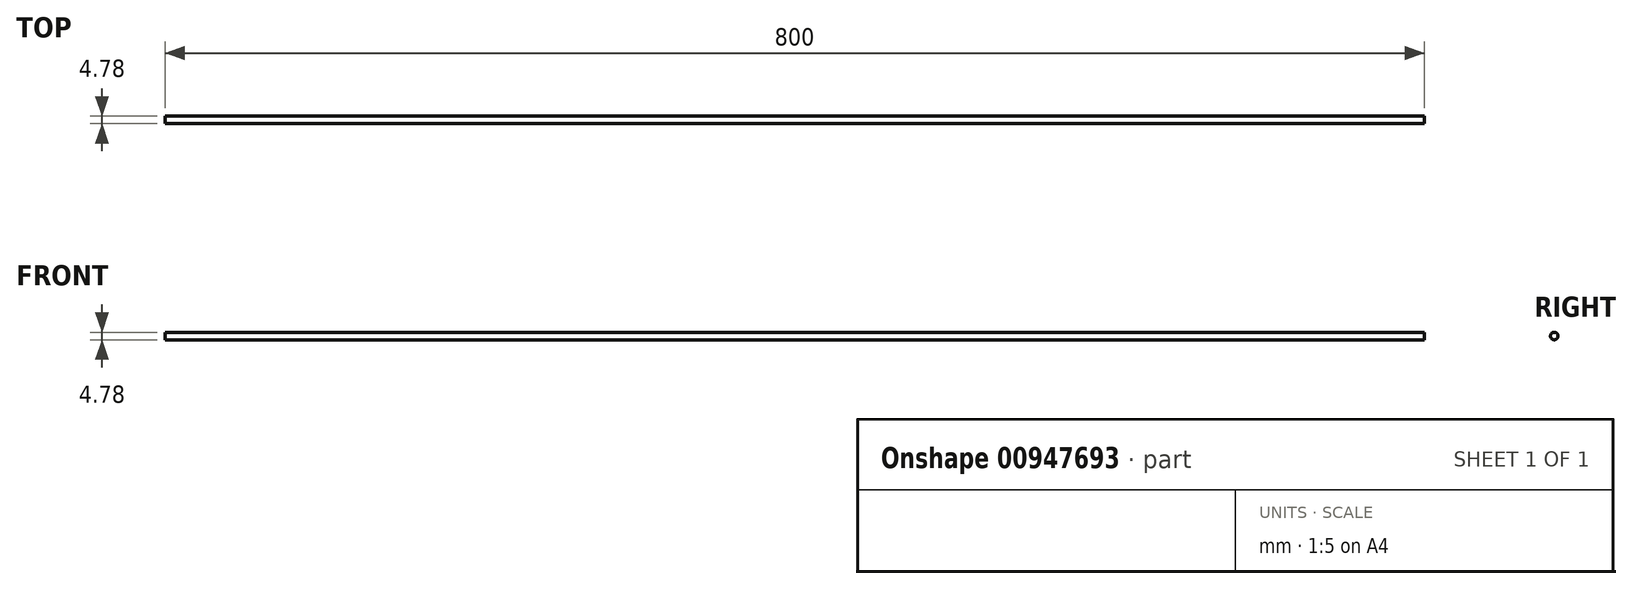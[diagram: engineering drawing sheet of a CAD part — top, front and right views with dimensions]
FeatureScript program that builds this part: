
annotation { "Feature Type Name" : "Feature", "Feature Type Description" : "" }
export const myFeature = defineFeature(function(context is Context, id is Id, definition is map)
    precondition{}
    {
        {
            var Q0;
            Q0=qCreatedBy(makeId("Right.planeOp"),FACE);
            var sketch = newSketch(context, id + "F0", { "sketchPlane" : qUnion([Q0])});
            skCircle(sketch, "E0", {"center": v(0, 0) * mm, "radius": 2.39 * mm});
            skSolve(sketch);
        }
        {
            var Q0;
            Q0 = qSketchRegion(id + "F0", true);
            extrude(context, id + "F1", {"entities" : qUnion([Q0]), "depth" : 800 * mm, "offsetDistance" : 25 * mm});
        }
    });
